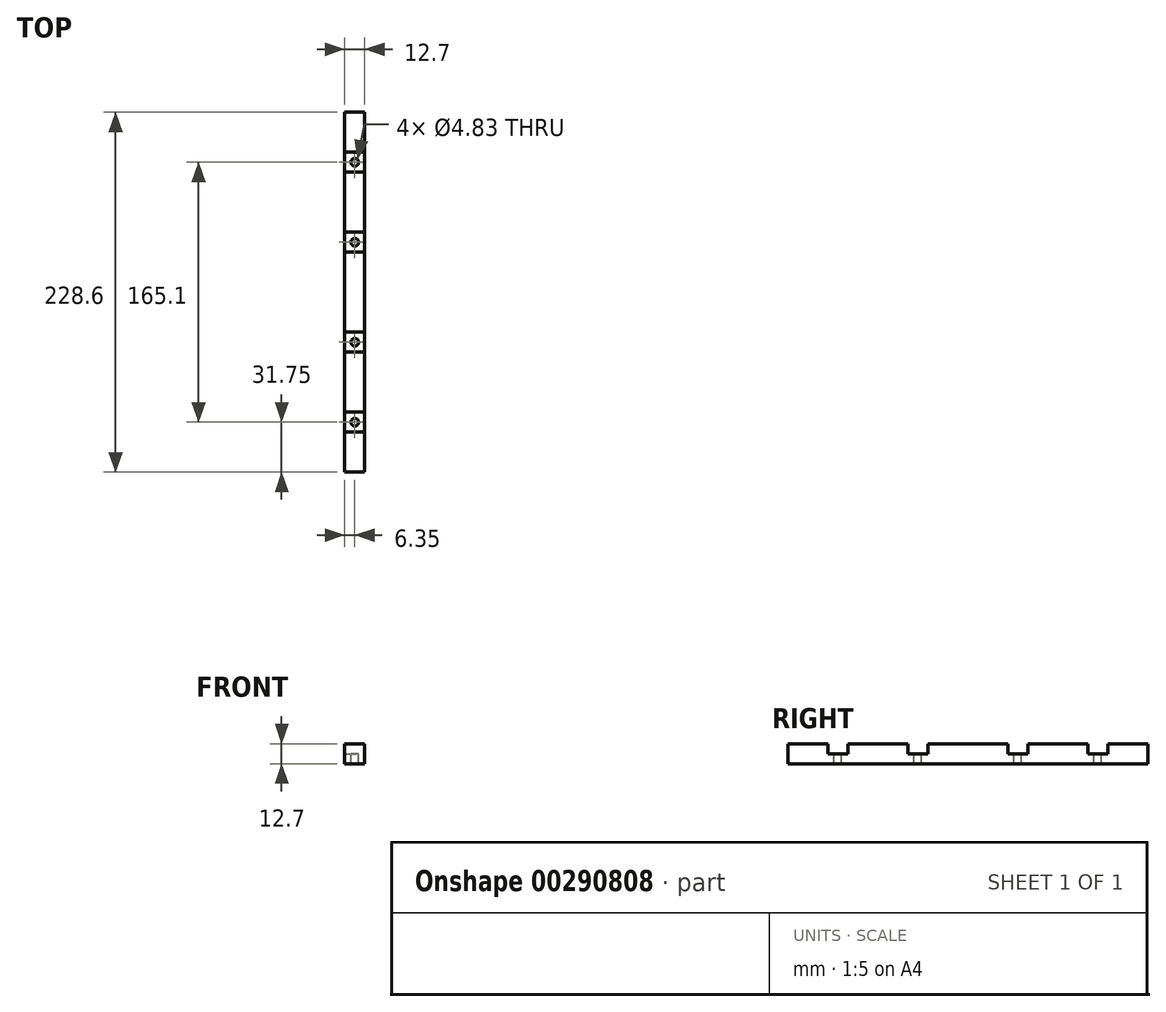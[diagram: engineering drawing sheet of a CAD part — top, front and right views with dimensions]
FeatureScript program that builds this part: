
annotation { "Feature Type Name" : "Feature", "Feature Type Description" : "" }
export const myFeature = defineFeature(function(context is Context, id is Id, definition is map)
    precondition{}
    {
        {
            var Q0;
            Q0=qCreatedBy(makeId("Top.planeOp"),FACE);
            var sketch = newSketch(context, id + "F0", { "sketchPlane" : qUnion([Q0])});
            skLineSegment(sketch, "E0.bottom", {"start": v(-12.7, 114.3) * mm, "end": v(0, 114.3) * mm});
            skLineSegment(sketch, "E0.top", {"start": v(-12.7, -114.3) * mm, "end": v(0, -114.3) * mm});
            skLineSegment(sketch, "E0.left", {"start": v(-12.7, 114.3) * mm, "end": v(-12.7, -114.3) * mm});
            skLineSegment(sketch, "E0.right", {"start": v(0, 114.3) * mm, "end": v(0, -114.3) * mm});
            skSolve(sketch);
        }
        {
            var Q0;
            Q0 = qSketchRegion(id + "F0", true);
            extrude(context, id + "F1", {"entities" : qUnion([Q0]), "depth" : 12.7 * mm});
        }
        {
            var Q0;
            Q0=makeQuery(id+"F1.opExtrude","SWEPT_FACE",FACE,{"disambiguationData":[OSD([sQuery(id+"F0.wireOp",EDGE,"E0.right")])]});
            var sketch = newSketch(context, id + "F2", { "sketchPlane" : qUnion([Q0])});
            skLineSegment(sketch, "E1.bottom", {"start": v(76.2, 12.7) * mm, "end": v(88.9, 12.7) * mm});
            skLineSegment(sketch, "E1.top", {"start": v(76.2, 6.35) * mm, "end": v(88.9, 6.35) * mm});
            skLineSegment(sketch, "E1.left", {"start": v(76.2, 12.7) * mm, "end": v(76.2, 6.35) * mm});
            skLineSegment(sketch, "E1.right", {"start": v(88.9, 12.7) * mm, "end": v(88.9, 6.35) * mm});
            skLineSegment(sketch, "E2.1.0.0", {"start": v(38.1, 12.7) * mm, "end": v(38.1, 6.35) * mm});
            skLineSegment(sketch, "E2.1.0.1", {"start": v(25.4, 6.35) * mm, "end": v(38.1, 6.35) * mm});
            skLineSegment(sketch, "E2.1.0.2", {"start": v(25.4, 12.7) * mm, "end": v(38.1, 12.7) * mm});
            skLineSegment(sketch, "E2.1.0.3", {"start": v(25.4, 12.7) * mm, "end": v(25.4, 6.35) * mm});
            skLineSegment(sketch, "E2.direction1", {"start": v(76.2, 6.35) * mm, "end": v(25.4, 6.35) * mm, "construction": true});
            skLineSegment(sketch, "E3.1.0.0", {"start": v(-38.1, 12.7) * mm, "end": v(-25.4, 12.7) * mm});
            skLineSegment(sketch, "E3.1.0.1", {"start": v(-76.2, 12.7) * mm, "end": v(-76.2, 6.35) * mm});
            skLineSegment(sketch, "E3.1.0.2", {"start": v(-88.9, 12.7) * mm, "end": v(-88.9, 6.35) * mm});
            skLineSegment(sketch, "E3.1.0.3", {"start": v(-25.4, 12.7) * mm, "end": v(-25.4, 6.35) * mm});
            skLineSegment(sketch, "E3.1.0.4", {"start": v(-38.1, 6.35) * mm, "end": v(-25.4, 6.35) * mm});
            skLineSegment(sketch, "E3.1.0.5", {"start": v(-88.9, 6.35) * mm, "end": v(-76.2, 6.35) * mm});
            skLineSegment(sketch, "E3.1.0.6", {"start": v(-88.9, 12.7) * mm, "end": v(-76.2, 12.7) * mm});
            skLineSegment(sketch, "E3.1.0.7", {"start": v(-38.1, 12.7) * mm, "end": v(-38.1, 6.35) * mm});
            skLineSegment(sketch, "E3.direction1", {"start": v(25.4, 6.35) * mm, "end": v(-88.9, 6.35) * mm, "construction": true});
            skSolve(sketch);
        }
        {
            var Q0;
            Q0 = qSketchRegion(id + "F2", true);
            extrude(context, id + "F3", {"entities" : qUnion([Q0]), "operationType" : NewBodyOperationType.REMOVE, "endBound" : BoundingType.THROUGH_ALL, "oppositeDirection" : true, "depth" : 25.4 * mm});
        }
        {
            var Q0;
            Q0=makeQuery(id+"F3.boolean.opBoolean","COPY",FACE,{"derivedFrom":makeQuery(id+"F3.opExtrude","SWEPT_FACE",FACE,{"disambiguationData":[OSD([sQuery(id+"F2.wireOp",EDGE,"E1.top")])]})});
            var sketch = newSketch(context, id + "F4", { "sketchPlane" : qUnion([Q0])});
            skCircle(sketch, "E4", {"center": v(-6.35, 82.55) * mm, "radius": 2.41 * mm});
            skCircle(sketch, "E5.0.1.0", {"center": v(-6.35, 31.75) * mm, "radius": 2.41 * mm});
            skCircle(sketch, "E5.1.1.0", {"center": v(-6.35, 31.75) * mm, "radius": 2.41 * mm});
            skCircle(sketch, "E5.2.1.0", {"center": v(-6.35, 31.75) * mm, "radius": 2.41 * mm});
            skLineSegment(sketch, "E5.direction1", {"start": v(-6.35, 82.55) * mm, "end": v(-6.35, 82.55) * mm});
            skLineSegment(sketch, "E5.direction2", {"start": v(-6.35, 82.55) * mm, "end": v(-6.35, 31.75) * mm, "construction": true});
            skCircle(sketch, "E6.0.1.0", {"center": v(-6.35, -31.75) * mm, "radius": 2.41 * mm});
            skCircle(sketch, "E6.0.1.1", {"center": v(-6.35, -82.55) * mm, "radius": 2.41 * mm});
            skLineSegment(sketch, "E6.direction1", {"start": v(-6.35, 31.75) * mm, "end": v(-6.35, 31.75) * mm});
            skLineSegment(sketch, "E6.direction2", {"start": v(-6.35, 31.75) * mm, "end": v(-6.35, -82.55) * mm, "construction": true});
            skSolve(sketch);
        }
        {
            var Q0;
            Q0 = qSketchRegion(id + "F4", true);
            extrude(context, id + "F5", {"entities" : qUnion([Q0]), "operationType" : NewBodyOperationType.REMOVE, "endBound" : BoundingType.THROUGH_ALL, "oppositeDirection" : true, "depth" : 25.4 * mm});
        }
    });
